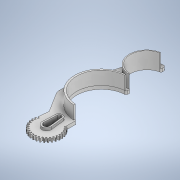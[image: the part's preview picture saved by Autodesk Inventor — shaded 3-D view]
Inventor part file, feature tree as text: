
AUTODESK INVENTOR PART (.ipt)
format: ipt  version: 2021 (Build 250183000, 183)  size: 572,416 bytes
history: native  units: mm
features: extrude x12, sketch x11, fillet x8
ambient origin geometry x8: Origin, YZ Plane, XZ Plane, XY Plane, X Axis, Y Axis, Z Axis, Center Point
bodies: Solid1 (feature_tree)
feature tree (31):
  extrude  "Extrusion1"  Depth=30.0mm
  extrude  "Extrusion4"  Depth=0.5mm
  sketch  "Sketch7"  dims[d12=15.0mm d13=60.0mm]
  extrude  "Extrusion2"  Depth=0.1mm TaperAngle=360.0deg
  extrude  "Extrusion7"  Depth=15.0mm
  extrude  "Extrusion8"  Depth=10.0mm
  extrude  "Extrusion9"  Depth=0.1mm
  fillet  "Fillet4"  Radius=0.1mm
  extrude  "Extrusion10"  Depth=3.0mm TaperAngle=0.0deg
  fillet  "Fillet5"  Radius=3.0mm
  fillet  "Fillet6"  Radius=5.0mm
  fillet  "Fillet7"  Radius=10.0mm
  fillet  "Fillet9"  Radius=40.0mm
  fillet  "Fillet10"  Radius=15.0mm
  extrude  "Extrusion11"  Depth=16.0mm
  fillet  "Fillet11"  Radius=40.0mm
  extrude  "Extrusion12"  Depth=16.0mm
  fillet  "Fillet12"  Radius=16.0mm
  extrude  "Extrusion13"  Depth=4.0mm TaperAngle=0.0deg
  extrude  "Extrusion3"  Depth=21.0mm
  extrude  "Extrusion5"  Depth=10.0mm
  sketch  "Sketch6"  dims[d6=0.1mm d7=310.0mm d9=360.0deg]
  sketch  "Sketch4"  dims[d0=30.0mm d1=35.0mm]
  sketch  "Sketch5"  dims[d2=0.5mm d4=0.5mm]
  sketch  "Sketch9"  dims[d14=30.0mm d15=10.0mm]
  sketch  "Sketch10"  dims[d19=4.0mm d20=0.0mm d22=7.5mm d23=0.1mm]
  sketch  "Sketch11"  dims[d24=2.0mm d25=3.0mm d26=0.0mm d27=3.0mm d28=0.0mm d29=5.0mm d30=10.0mm d31=0.0mm d32=40.0mm d33=15.0mm d34=0.0mm]
  sketch  "Sketch12"  dims[d40=16.0mm d41=0.0mm d42=40.0mm d43=40.0mm]
  sketch  "Sketch13"  dims[d44=4.0mm d45=0.0mm d46=40.0mm d47=16.0mm d48=0.0mm]
  sketch  "Sketch14"  dims[d49=2.0mm d50=4.0mm d51=0.0mm]
  sketch  "Sketch15"  dims[d52=234.0mm d53=21.0mm d54=10.0mm d56=2.0mm d57=1.75mm d58=4.0mm d59=0.0mm d60=1.75mm d61=16.0mm d62=0.0mm d63=2.0mm d64=3.0mm d65=0.0mm d11=0.5mm]
